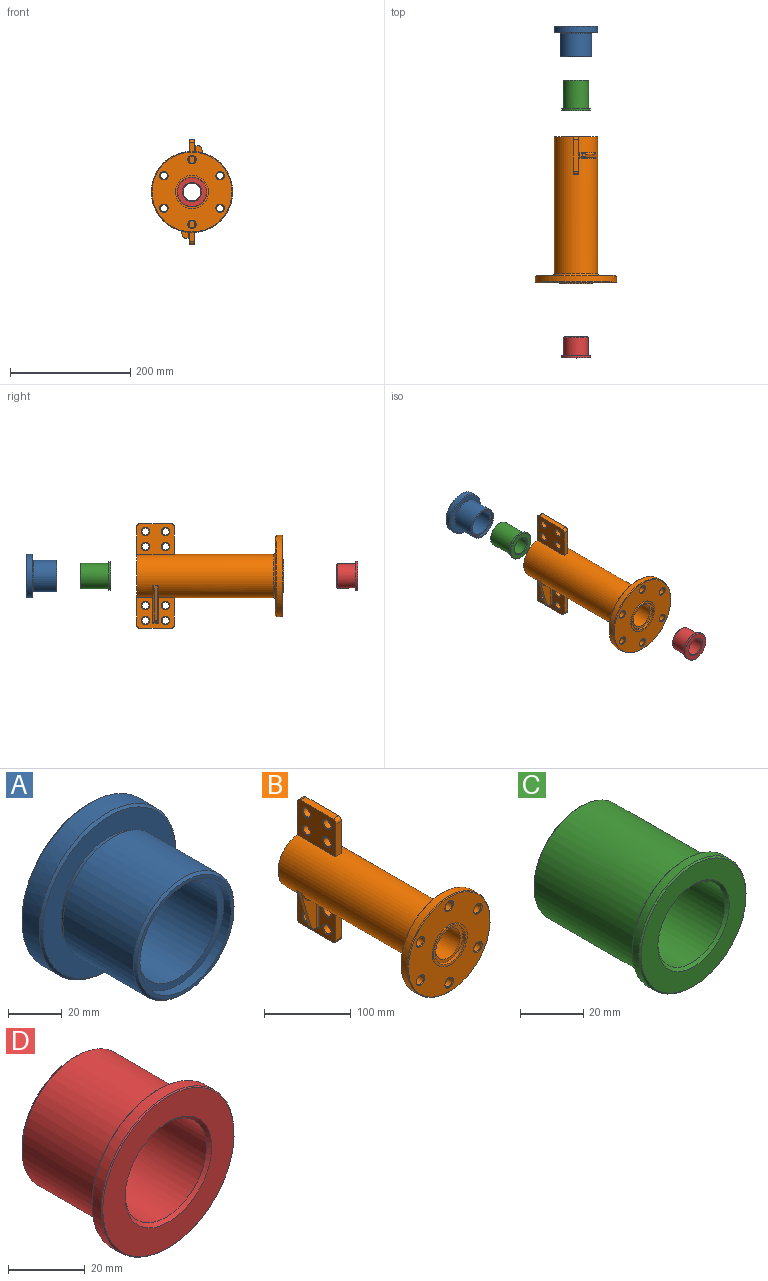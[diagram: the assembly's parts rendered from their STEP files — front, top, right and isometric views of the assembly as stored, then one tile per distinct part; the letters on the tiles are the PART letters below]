
ASSEMBLY  parts=4 mates=3
PART A: 13 faces, bbox 72x51x72 mm
  f0: cylinder r=21mm len=47mm, axis (0,-1,0), area 6201.5mm2, adj f2,f11
  f1: plane 51x51mm, normal (0,-1,0), area 233.3mm2, adj f8,f12
  f2: plane 70x70mm, normal (0,1,0), area 2463mm2, adj f0,f9
  f3: cylinder r=36mm len=72mm, axis (0,-1,0), area 2035.8mm2, adj f9,f10
  f4: plane 70x70mm, normal (0,-1,0), area 1805.6mm2, adj f5,f10
  f5: cylinder r=25.5mm len=51mm, axis (0,-1,0), area 320.4mm2, adj f4,f6
  f6: plane 53x53mm, normal (0,1,0), area 163.4mm2, adj f5,f7
  f7: cylinder r=26.5mm len=53mm, axis (0,-1,0), area 6160.7mm2, adj f6,f8
  f8: cone r=25.5mm half-angle=45deg, axis (0,1,0), area 231mm2, adj f1,f7
  f9: cone r=36mm half-angle=45deg, axis (0,-1,0), area 315.4mm2, adj f2,f3
  f10: cone r=35mm half-angle=45deg, axis (0,1,0), area 315.4mm2, adj f3,f4
  f11: plane 48x48mm, normal (0,-1,0), area 424.1mm2, adj f0,f12
  f12: cylinder r=24mm len=48mm, axis (0,-1,0), area 603.2mm2, adj f1,f11
PART B: 93 faces, bbox 135x245x174 mm
  f0: cylinder r=36mm len=228mm, axis (0,1,0), area 49777.2mm2, adj f1,f18,f28,f30,f31,f32,f33,f34
  f1: plane 63x51.28mm, normal (-1,0,0), area 2249.4mm2, adj f0,f18,f33,f35,f44,f46,f48,f50
  f2: cone r=7mm half-angle=45deg, axis (0,1,0), area 57.8mm2, adj f4,f19
  f3: cone r=6mm half-angle=45deg, axis (0,-1,0), area 57.8mm2, adj f4,f21
  f4: cylinder r=6mm len=12mm, axis (0,-1,0), area 377mm2, adj f2,f3
  f5: cone r=7mm half-angle=45deg, axis (0,1,0), area 57.8mm2, adj f7,f19
  f6: cone r=6mm half-angle=45deg, axis (0,-1,0), area 57.8mm2, adj f7,f21
  f7: cylinder r=6mm len=12mm, axis (0,-1,0), area 377mm2, adj f5,f6
  f8: cone r=7mm half-angle=45deg, axis (0,1,0), area 57.8mm2, adj f10,f19
  f9: cone r=6mm half-angle=45deg, axis (0,-1,0), area 57.8mm2, adj f10,f21
  f10: cylinder r=6mm len=12mm, axis (0,-1,0), area 377mm2, adj f8,f9
  f11: cone r=7mm half-angle=45deg, axis (0,1,0), area 57.8mm2, adj f13,f19
  f12: cone r=6mm half-angle=45deg, axis (0,-1,0), area 57.8mm2, adj f13,f21
  f13: cylinder r=6mm len=12mm, axis (0,-1,0), area 377mm2, adj f11,f12
  f14: cone r=7mm half-angle=45deg, axis (0,1,0), area 57.8mm2, adj f16,f19
  f15: cone r=6mm half-angle=45deg, axis (0,-1,0), area 57.8mm2, adj f16,f21
  f16: cylinder r=6mm len=12mm, axis (0,-1,0), area 377mm2, adj f14,f15
  f17: plane 55x55mm, normal (0,-1,0), area 490.1mm2, adj f22,f92
  f18: plane 164x72mm, normal (0,1,0), area 2976.8mm2, adj f0,f1,f30,f31,f34,f62,f63,f84
  f19: plane 133x133mm, normal (0,1,0), area 8190.9mm2, adj f2,f5,f8,f11,f14,f25,f26,f28
  f20: cylinder r=67.5mm len=135mm, axis (0,1,0), area 4241.2mm2, adj f26,f27
  f21: plane 133x133mm, normal (0,-1,0), area 10593.5mm2, adj f3,f6,f9,f12,f15,f22,f24,f27
  f22: cylinder r=27.5mm len=55mm, axis (0,1,0), area 345.6mm2, adj f17,f21
  f23: cylinder r=6mm len=12mm, axis (0,-1,0), area 377mm2, adj f24,f25
  f24: cone r=6mm half-angle=45deg, axis (0,-1,0), area 57.8mm2, adj f21,f23
  f25: cone r=7mm half-angle=45deg, axis (0,1,0), area 57.8mm2, adj f19,f23
  f26: cone r=66.5mm half-angle=45deg, axis (0,-1,0), area 595.3mm2, adj f19,f20
  f27: cone r=67.5mm half-angle=45deg, axis (0,1,0), area 595.3mm2, adj f20,f21
  f28: torus R=39mm, axis (0,-1,0), area 1098.2mm2, adj f0,f19
  f29: plane 53x9mm, normal (0,0,1), area 477mm2, adj f30,f31,f60,f63
  f30: plane 63x51.28mm, normal (1,0,0), area 2249.4mm2, adj f0,f18,f29,f32,f53,f55,f57,f59
  f31: plane 63x51.28mm, normal (-1,0,0), area 2639mm2, adj f0,f18,f29,f32,f52,f54,f56,f58
  f32: plane 46.28x9mm, normal (0,-1,0), area 414.8mm2, adj f0,f30,f31,f60
  f33: plane 46.28x9mm, normal (0,-1,0), area 414.8mm2, adj f0,f1,f34,f61
  f34: plane 63x51.28mm, normal (1,0,0), area 2639mm2, adj f0,f18,f33,f35,f45,f47,f49,f51
  f35: plane 53x9mm, normal (0,0,-1), area 477mm2, adj f1,f34,f61,f62
  f36: cylinder r=6mm len=12mm, axis (1,0,0), area 279mm2, adj f48,f49
  f37: cylinder r=6mm len=12mm, axis (1,0,0), area 279mm2, adj f44,f45
  f38: cylinder r=6mm len=12mm, axis (1,0,0), area 279mm2, adj f46,f47
  f39: cylinder r=6mm len=12mm, axis (1,0,0), area 279mm2, adj f50,f51
  f40: cylinder r=6mm len=12mm, axis (1,0,0), area 279mm2, adj f58,f59
  f41: cylinder r=6mm len=12mm, axis (1,0,0), area 279mm2, adj f52,f53
  f42: cylinder r=6mm len=12mm, axis (1,0,0), area 279mm2, adj f54,f55
  f43: cylinder r=6mm len=12mm, axis (1,0,0), area 279mm2, adj f56,f57
  f44: cone r=6mm half-angle=45deg, axis (-1,0,0), area 45.5mm2, adj f1,f37
  f45: cone r=6.8mm half-angle=45deg, axis (1,0,0), area 45.5mm2, adj f34,f37
  f46: cone r=6mm half-angle=45deg, axis (-1,0,0), area 45.5mm2, adj f1,f38
  f47: cone r=6.8mm half-angle=45deg, axis (1,0,0), area 45.5mm2, adj f34,f38
  f48: cone r=6mm half-angle=45deg, axis (-1,0,0), area 45.5mm2, adj f1,f36
  f49: cone r=6.8mm half-angle=45deg, axis (1,0,0), area 45.5mm2, adj f34,f36
  f50: cone r=6mm half-angle=45deg, axis (-1,0,0), area 45.5mm2, adj f1,f39
  f51: cone r=6.8mm half-angle=45deg, axis (1,0,0), area 45.5mm2, adj f34,f39
  f52: cone r=6.8mm half-angle=45deg, axis (-1,0,0), area 45.5mm2, adj f31,f41
  f53: cone r=6mm half-angle=45deg, axis (1,0,0), area 45.5mm2, adj f30,f41
  f54: cone r=6.8mm half-angle=45deg, axis (-1,0,0), area 45.5mm2, adj f31,f42
  f55: cone r=6mm half-angle=45deg, axis (1,0,0), area 45.5mm2, adj f30,f42
  f56: cone r=6.8mm half-angle=45deg, axis (-1,0,0), area 45.5mm2, adj f31,f43
  f57: cone r=6mm half-angle=45deg, axis (1,0,0), area 45.5mm2, adj f30,f43
  f58: cone r=6.8mm half-angle=45deg, axis (-1,0,0), area 45.5mm2, adj f31,f40
  f59: cone r=6mm half-angle=45deg, axis (1,0,0), area 45.5mm2, adj f30,f40
  f60: cylinder r=5mm len=9mm, axis (1,0,0), area 70.7mm2, adj f29,f30,f31,f32
  f61: cylinder r=5mm len=9mm, axis (-1,0,0), area 70.7mm2, adj f1,f33,f34,f35
  f62: cylinder r=5mm len=9mm, axis (1,0,0), area 70.7mm2, adj f1,f18,f34,f35
  f63: cylinder r=5mm len=9mm, axis (-1,0,0), area 70.7mm2, adj f18,f29,f30,f31
  f64: plane 5x4.26mm, normal (0,0,1), area 21.3mm2, adj f66,f67,f73,f83
  f65: plane 58.41x17.17mm, normal (0.96,0,0.28), area 313.1mm2, adj f0,f66,f67,f73,f79,f80
  f66: plane 54.27x23.95mm, normal (0,1,0), area 637.4mm2, adj f64,f65,f73,f79,f81
  f67: plane 54.27x23.95mm, normal (0,-1,0), area 637.4mm2, adj f64,f65,f73,f80,f82
  f68: plane 5x4.26mm, normal (0,0,-1), area 21.3mm2, adj f70,f71,f72,f78
  f69: plane 58.41x17.17mm, normal (-0.96,0,-0.28), area 313.1mm2, adj f0,f70,f71,f72,f74,f75
  f70: plane 54.27x23.95mm, normal (0,1,0), area 637.4mm2, adj f68,f69,f72,f74,f76
  f71: plane 54.27x23.95mm, normal (0,-1,0), area 637.4mm2, adj f68,f69,f72,f75,f77
  f72: cylinder r=5mm len=5mm, axis (0,-1,0), area 32.1mm2, adj f68,f69,f70,f71
  f73: cylinder r=5mm len=5mm, axis (0,-1,0), area 32.1mm2, adj f64,f65,f66,f67
  f74: torus R=38mm, axis (0,1,0), area 104.5mm2, adj f0,f69,f70,f76
  f75: torus R=38mm, axis (0,1,0), area 104.5mm2, adj f0,f69,f71,f77
  f76: cylinder r=2mm len=43.28mm, axis (0,0,1), area 130mm2, adj f1,f70,f74,f78
  f77: cylinder r=2mm len=43.28mm, axis (0,0,-1), area 130mm2, adj f1,f71,f75,f78
  f78: cylinder r=2mm len=9mm, axis (0,1,0), area 20.3mm2, adj f1,f68,f76,f77
  f79: torus R=38mm, axis (0,1,0), area 104.5mm2, adj f0,f65,f66,f81
  f80: torus R=38mm, axis (0,1,0), area 104.5mm2, adj f0,f65,f67,f82
  f81: cylinder r=2mm len=43.28mm, axis (0,0,1), area 130mm2, adj f30,f66,f79,f83
  f82: cylinder r=2mm len=43.28mm, axis (0,0,-1), area 130mm2, adj f30,f67,f80,f83
  f83: cylinder r=2mm len=9mm, axis (0,-1,0), area 20.3mm2, adj f30,f64,f81,f82
  f84: cylinder r=24.75mm len=49.5mm, axis (0,1,0), area 6220.4mm2, adj f18,f85
  f85: plane 49.5x49.5mm, normal (0,1,0), area 667.8mm2, adj f84,f86
  f86: cylinder r=20mm len=40mm, axis (0,1,0), area 1540.6mm2, adj f85,f87
  f87: plane 56x56mm, normal (0,-1,0), area 1206.4mm2, adj f86,f88
  f88: cylinder r=28mm len=157.74mm, axis (0,1,0), area 27751.2mm2, adj f87,f89
  f89: plane 56x56mm, normal (0,1,0), area 1206.4mm2, adj f88,f90
  f90: cylinder r=20mm len=40mm, axis (0,1,0), area 3895.6mm2, adj f89,f91
  f91: plane 49x49mm, normal (0,-1,0), area 629.1mm2, adj f90,f92
  f92: cylinder r=24.5mm len=49mm, axis (0,1,0), area 615.8mm2, adj f17,f91
PART C: 11 faces, bbox 48x51x48 mm
  f0: plane 47x47mm, normal (0,-1,0), area 930.7mm2, adj f6,f10
  f1: cylinder r=15mm len=49mm, axis (0,-1,0), area 4618.1mm2, adj f9,f10
  f2: plane 41x41mm, normal (0,1,0), area 516mm2, adj f8,f9
  f3: cylinder r=21mm len=46.5mm, axis (0,-1,0), area 6135.5mm2, adj f4,f8
  f4: plane 47x47mm, normal (0,1,0), area 349.5mm2, adj f3,f7
  f5: cylinder r=24mm len=48mm, axis (0,-1,0), area 452.4mm2, adj f6,f7
  f6: cone r=23.5mm half-angle=45deg, axis (0,1,0), area 105.5mm2, adj f0,f5
  f7: cone r=24mm half-angle=45deg, axis (0,-1,0), area 105.5mm2, adj f4,f5
  f8: cone r=21mm half-angle=45deg, axis (0,-1,0), area 92.2mm2, adj f2,f3
  f9: cone r=16mm half-angle=45deg, axis (0,1,0), area 137.7mm2, adj f1,f2
  f10: cone r=15mm half-angle=45deg, axis (0,-1,0), area 137.7mm2, adj f0,f1
PART D: 11 faces, bbox 49x35x49 mm
  f0: plane 48.4x48.4mm, normal (0,-1,0), area 1035.6mm2, adj f8,f10
  f1: cylinder r=15mm len=33mm, axis (0,1,0), area 3110.2mm2, adj f7,f8
  f2: plane 38x38mm, normal (0,1,0), area 329.9mm2, adj f6,f7
  f3: cylinder r=20mm len=40mm, axis (0,1,0), area 3769.9mm2, adj f4,f6
  f4: plane 48.4x48.4mm, normal (0,1,0), area 583.2mm2, adj f3,f9
  f5: cylinder r=24.5mm len=49mm, axis (0,1,0), area 523.4mm2, adj f9,f10
  f6: cone r=19mm half-angle=45deg, axis (0,-1,0), area 173.3mm2, adj f2,f3
  f7: cone r=15mm half-angle=45deg, axis (0,1,0), area 137.7mm2, adj f1,f2
  f8: cone r=16mm half-angle=45deg, axis (0,-1,0), area 137.7mm2, adj f0,f1
  f9: cone r=24.2mm half-angle=45deg, axis (0,-1,0), area 64.9mm2, adj f4,f5
  f10: cone r=24.5mm half-angle=45deg, axis (0,1,0), area 64.9mm2, adj f0,f5
PLACE A t=(-69.31,173.13,-15.13)mm
PLACE B t=(-69.31,0,-15.13)mm
PLACE C t=(-69.31,82.75,-15.13)mm
PLACE D rot(axis=(0,1,0),0deg) t=(-69.31,-123.41,-15.13)mm
MATE cylindrical A.f0 <-> C.f1  axis (0,-1,0) through (-69.31,382.13,-15.13)mm
MATE cylindrical D.f1 <-> B.f0  axis (0,1,0) through (-69.31,-89.41,-15.13)mm
MATE slider A.f3 <-> B.f0  axis (0,1,0) through (-69.31,428.13,-15.13)mm
